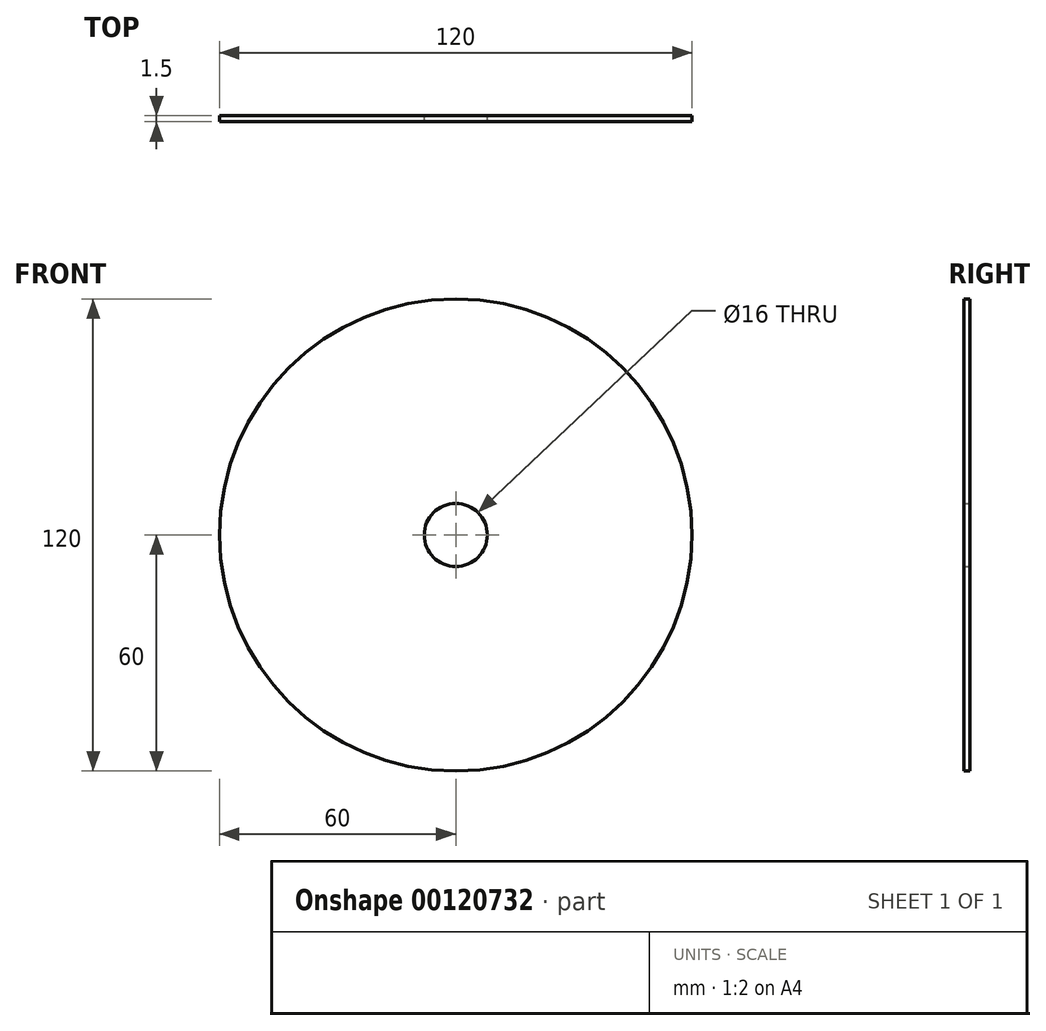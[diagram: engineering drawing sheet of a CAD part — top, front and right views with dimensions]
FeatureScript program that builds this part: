
annotation { "Feature Type Name" : "Feature", "Feature Type Description" : "" }
export const myFeature = defineFeature(function(context is Context, id is Id, definition is map)
    precondition{}
    {
        {
            var Q0;
            Q0=qCreatedBy(makeId("Front.planeOp"),FACE);
            var sketch = newSketch(context, id + "F0", { "sketchPlane" : qUnion([Q0])});
            skCircle(sketch, "E0", {"center": v(0, 0) * mm, "radius": 60 * mm});
            skCircle(sketch, "E1", {"center": v(0, 0) * mm, "radius": 8 * mm});
            skSolve(sketch);
        }
        {
            var Q0;
            Q0=makeQuery(id+"F0.imprint","IMPRINT",FACE,{"disambiguationData":[TD([[makeQuery(id+"F0.imprint","IMPRINT",EDGE,{"derivedFrom":sQuery(id+"F0.wireOp",EDGE,"E0")}),1.0]])]});
            extrude(context, id + "F1", {"entities" : qUnion([Q0]), "depth" : 1.5 * mm});
        }
    });
